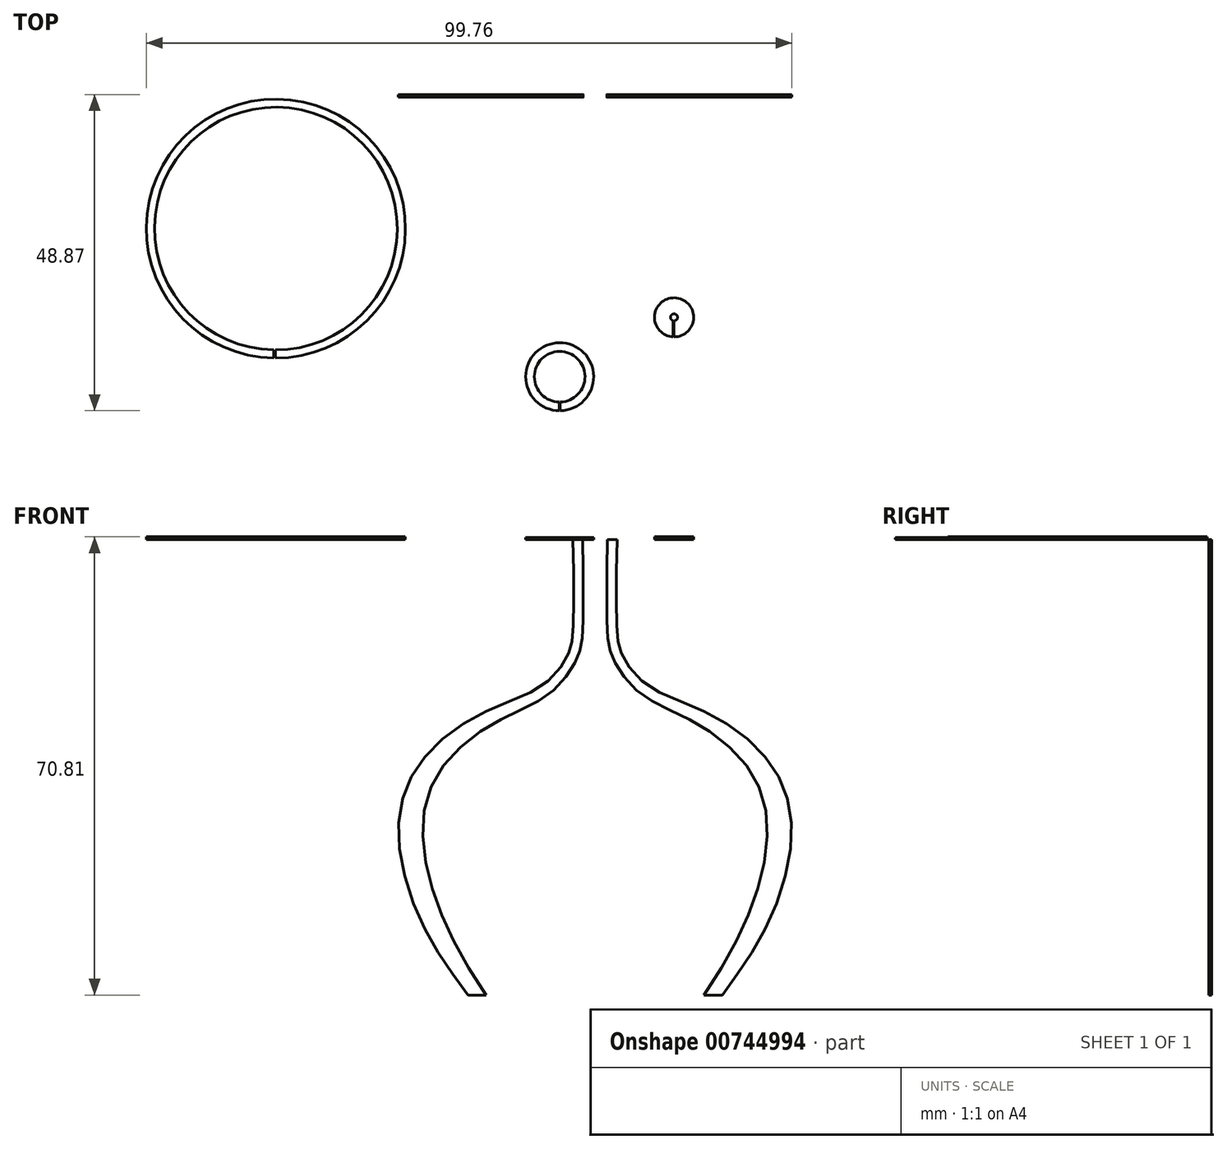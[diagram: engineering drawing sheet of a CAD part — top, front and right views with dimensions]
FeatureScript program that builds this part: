
annotation { "Feature Type Name" : "Feature", "Feature Type Description" : "" }
export const myFeature = defineFeature(function(context is Context, id is Id, definition is map)
    precondition{}
    {
        {
            var Q0;
            Q0=qCreatedBy(makeId("Front.planeOp"),FACE);
            var sketch = newSketch(context, id + "F0", { "sketchPlane" : qUnion([Q0])});
            skFitSpline(sketch, "E0", {"points": [v(1.88, 0) * mm, v(1.93, -14.64) * mm, v(2.8, -18.44) * mm, v(6.86, -23.7) * mm, v(15.33, -28.2) * mm, v(25.15, -37.75) * mm, v(25.57, -52.47) * mm, v(16.82, -70.41) * mm], "startDerivative": vector(0.15, -109.11) * mm, "endDerivative": vector(-67.3, -99) * mm});
            skLineSegment(sketch, "E1", {"start": v(1.88, 0) * mm, "end": v(3.42, 0) * mm});
            skLineSegment(sketch, "E2", {"start": v(16.82, -70.41) * mm, "end": v(19.65, -70.41) * mm});
            skFitSpline(sketch, "E3", {"points": [v(3.42, 0) * mm, v(3.42, -14.49) * mm, v(4.08, -17.6) * mm, v(7.76, -22.29) * mm, v(17.35, -26.78) * mm, v(26.94, -34.43) * mm, v(30.41, -44.74) * mm, v(26.84, -59.13) * mm, v(19.65, -70.41) * mm], "startDerivative": vector(-3.58, -116.19) * mm, "endDerivative": vector(-54.32, -73.83) * mm});
            skSolve(sketch);
        }
        {
            var Q0;
            Q0=makeQuery(id+"F0.imprint","IMPRINT",FACE,{"disambiguationData":[TD([[makeQuery(id+"F0.imprint","IMPRINT",EDGE,{"derivedFrom":sQuery(id+"F0.wireOp",EDGE,"E0")}),1.0]])]});
            extrude(context, id + "F1", {"entities" : qUnion([Q0]), "depth" : 0.4 * mm});
        }
        {
            var Q0;
            Q0=qCreatedBy(makeId("Top.planeOp"),FACE);
            var sketch = newSketch(context, id + "F2", { "sketchPlane" : qUnion([Q0])});
            skArc(sketch, "E4", {"start": v(-49.42, -40.73) * mm, "mid": v(-49.13, -0.69) * mm, "end": v(-49.65, -40.72) * mm});
            skArc(sketch, "E5", {"start": v(-49.42, -39.47) * mm, "mid": v(-49.13, -1.95) * mm, "end": v(-49.65, -39.46) * mm});
            skLineSegment(sketch, "E6", {"start": v(-49.65, -40.72) * mm, "end": v(-49.65, -39.46) * mm});
            skLineSegment(sketch, "E7", {"start": v(-49.42, -39.47) * mm, "end": v(-49.42, -40.73) * mm});
            skSolve(sketch);
        }
        {
            var Q0;
            Q0=makeQuery(id+"F2.imprint","IMPRINT",FACE,{"disambiguationData":[TD([[makeQuery(id+"F2.imprint","IMPRINT",EDGE,{"derivedFrom":sQuery(id+"F2.wireOp",EDGE,"E4")}),1.0]])]});
            extrude(context, id + "F3", {"entities" : qUnion([Q0]), "depth" : .4 * mm});
        }
        {
            var Q0;
            Q0=makeQuery(id+"F1.opExtrude","SWEPT_BODY",BODY,{"disambiguationData":[OSD([sQuery(id+"F0.wireOp",EDGE,"E0"),sQuery(id+"F0.wireOp",EDGE,"E1"),sQuery(id+"F0.wireOp",EDGE,"E2"),sQuery(id+"F0.wireOp",EDGE,"E3")])]});
            var Q1;
            Q1=qCreatedBy(makeId("Right.planeOp"),FACE);
            mirror(context, id + "F4", {"entities" : qUnion([Q0]), "mirrorPlane" : qUnion([Q1])});
        }
        {
            var Q0;
            Q0=qCreatedBy(makeId("Top.planeOp"),FACE);
            var sketch = newSketch(context, id + "F5", { "sketchPlane" : qUnion([Q0])});
            skArc(sketch, "E8", {"start": v(-5.38, -48.87) * mm, "mid": v(-5.48, -38.36) * mm, "end": v(-5.5, -48.87) * mm});
            skArc(sketch, "E9", {"start": v(-5.38, -47.52) * mm, "mid": v(-5.48, -39.7) * mm, "end": v(-5.5, -47.52) * mm});
            skLineSegment(sketch, "E10", {"start": v(-5.5, -48.87) * mm, "end": v(-5.5, -47.52) * mm});
            skLineSegment(sketch, "E11", {"start": v(-5.38, -48.87) * mm, "end": v(-5.38, -47.52) * mm});
            skSolve(sketch);
        }
        {
            var Q0;
            Q0=qSketchRegion(id+"F5",true);
            extrude(context, id + "F6", {"entities" : qUnion([Q0]), "depth" : .3 * mm});
        }
        {
            var Q0;
            Q0=qCreatedBy(makeId("Top.planeOp"),FACE);
            var sketch = newSketch(context, id + "F7", { "sketchPlane" : qUnion([Q0])});
            skArc(sketch, "E12", {"start": v(12.19, -37.45) * mm, "mid": v(12.29, -31.4) * mm, "end": v(12.08, -37.45) * mm});
            skArc(sketch, "E13", {"start": v(12.19, -34.97) * mm, "mid": v(12.29, -33.9) * mm, "end": v(12.08, -34.95) * mm});
            skLineSegment(sketch, "E14", {"start": v(12.08, -37.45) * mm, "end": v(12.08, -34.95) * mm});
            skLineSegment(sketch, "E15", {"start": v(12.19, -37.45) * mm, "end": v(12.19, -34.95) * mm});
            skSolve(sketch);
        }
        {
            var Q0;
            Q0=qSketchRegion(id+"F7",true);
            extrude(context, id + "F8", {"entities" : qUnion([Q0]), "depth" : .4 * mm});
        }
        {
            var Q0;
            Q0=makeQuery(id+"F2.imprint","IMPRINT",FACE,{"disambiguationData":[TD([[makeQuery(id+"F2.imprint","IMPRINT",EDGE,{"derivedFrom":sQuery(id+"F2.wireOp",EDGE,"E4")}),1.0]])]});
            extrude(context, id + "F9", {"entities" : qUnion([Q0]), "depth" : .4 * mm});
        }
    });
